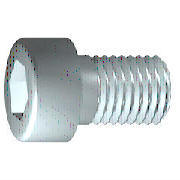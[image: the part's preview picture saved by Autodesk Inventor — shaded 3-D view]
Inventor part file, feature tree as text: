
AUTODESK INVENTOR PART (.ipt)
format: ipt  version: 2020 (Build 240168000, 168)  size: 188,416 bytes
history: native  units: mm (DEFAULTED — no unit token found)
features: sketch x2, extrude x1, plane x1, fillet x1
ambient origin geometry x7: Origin, YZ Plane, XY Plane, X Axis, Y Axis, Z Axis, Center Point
bodies: Solid1 (feature_tree), Body (feature_tree)
feature tree (5):
  extrude  "Slot"  Depth=4.0mm
  plane  "Work Plane1"
  fillet  "Fillet2"  Radius=4.0mm
  sketch  "Sketch1"  dims[d1=20.0mm d2=0.429515mm d3=4.0mm]
  sketch  "Sketch2"  dims[d4=2.0mm d5=60.0deg d6=4.0mm d7=4.0mm d8=3.464102mm d9=7.0mm d10=90.0deg d11=10.0mm d12=0.0mm d13=20.0mm d14=0.0mm d15=0.429415mm d16=0.429415mm d17=0.4mm d19=0.0mm d26=40.0mm d27=45.0deg d28=0.0mm d29=0.0mm d30=0.2mm]
